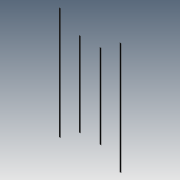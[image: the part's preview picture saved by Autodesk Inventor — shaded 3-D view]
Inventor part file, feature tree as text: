
AUTODESK INVENTOR PART (.ipt)
format: ipt  version: 2012 (Build 160160000, 160)  size: 84,992 bytes
history: native  units: in
note: dims shown in document units (in); Inventor stores cm internally (conversion verified against a paired STEP export)
features: extrude x1, sketch x1
ambient origin geometry x8: Origin, YZ Plane, XZ Plane, XY Plane, X Axis, Y Axis, Z Axis, Center Point
bodies: Solid1 (feature_tree)
feature tree (2):
  extrude  "Extrusion1"  Depth=84.0in
  sketch  "Sketch1"  dims[d0=14.0in d1=84.0in d2=63.0in d3=1.0in d4=10.5in d5=15.5in d6=14.0in d7=0.0625in d8=0.0in]
